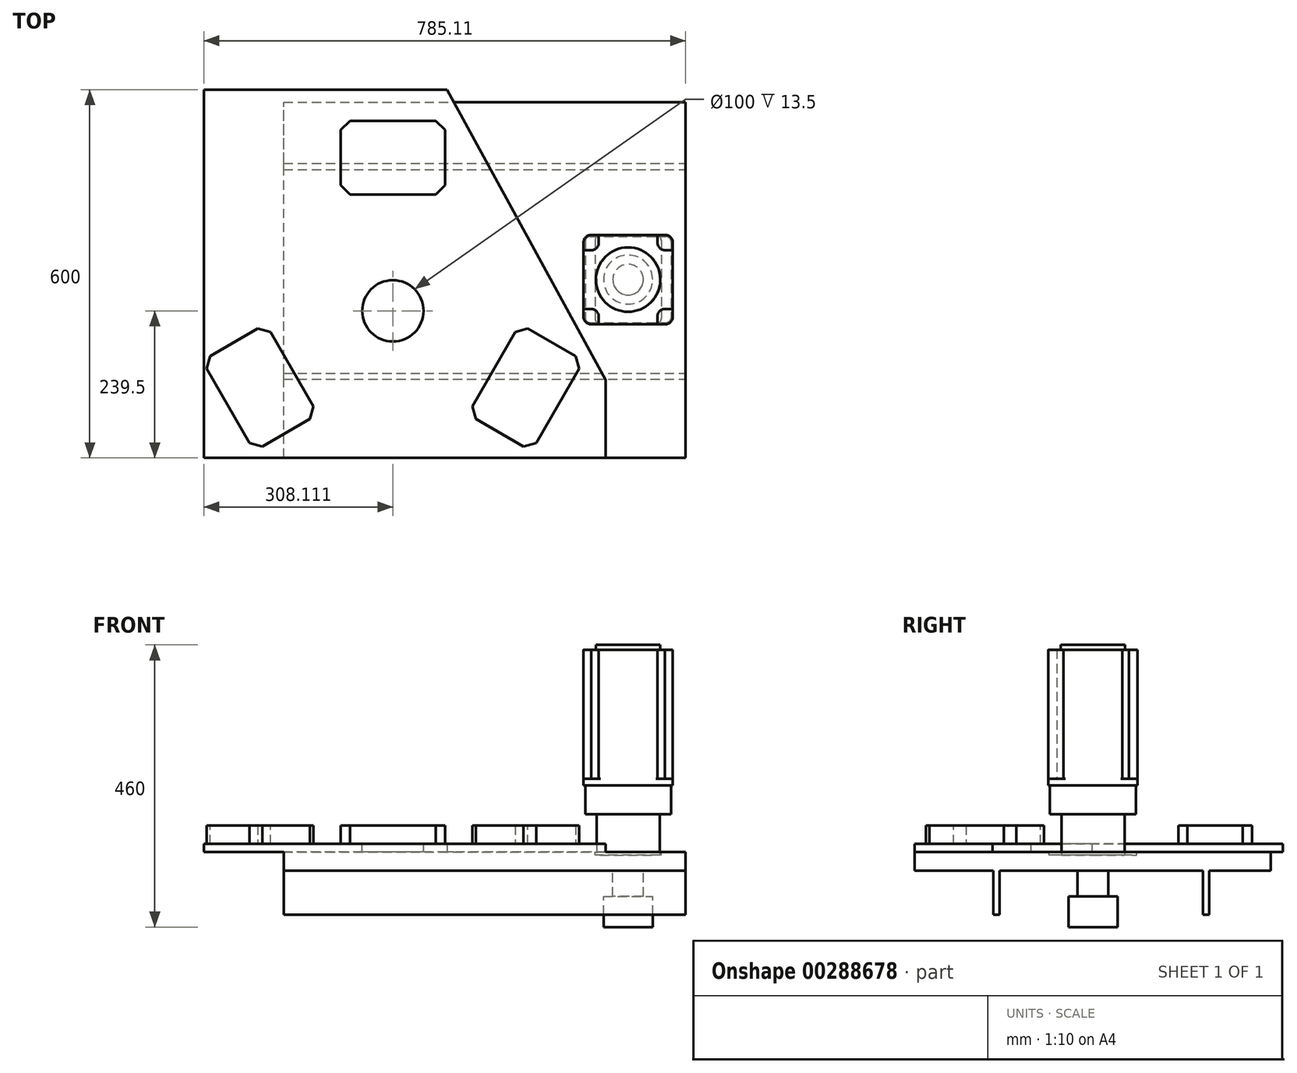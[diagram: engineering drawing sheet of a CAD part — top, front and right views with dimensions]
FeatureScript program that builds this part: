
annotation { "Feature Type Name" : "Feature", "Feature Type Description" : "" }
export const myFeature = defineFeature(function(context is Context, id is Id, definition is map)
    precondition{}
    {
        {
            var Q0;
            Q0=qCreatedBy(makeId("Front.planeOp"),FACE);
            var sketch = newSketch(context, id + "F0", { "sketchPlane" : qUnion([Q0])});
            skLineSegment(sketch, "E0.bottom", {"start": v(-291.9, 30) * mm, "end": v(363.1, 30) * mm});
            skLineSegment(sketch, "E0.top", {"start": v(-291.9, 0) * mm, "end": v(363.1, 0) * mm});
            skLineSegment(sketch, "E0.left", {"start": v(-291.9, 30) * mm, "end": v(-291.9, 0) * mm});
            skLineSegment(sketch, "E0.right", {"start": v(363.1, 30) * mm, "end": v(363.1, 0) * mm});
            skSolve(sketch);
        }
        {
            var Q0;
            Q0 = qSketchRegion(id + "F0", true);
            extrude(context, id + "F1", {"entities" : qUnion([Q0]), "depth" : 580 * mm});
        }
        {
            var Q0;
            Q0=makeQuery(id+"F1.opExtrude","SWEPT_FACE",FACE,{"disambiguationData":[OSD([sQuery(id+"F0.wireOp",EDGE,"E0.bottom")])]});
            var sketch = newSketch(context, id + "F2", { "sketchPlane" : qUnion([Q0])});
            skLineSegment(sketch, "E1.0.0", {"start": v(363.1, 0) * mm, "end": v(-291.9, 0) * mm, "construction": true});
            skLineSegment(sketch, "E1.0.1", {"start": v(-291.9, 0) * mm, "end": v(-291.9, -580) * mm, "construction": true});
            skLineSegment(sketch, "E1.0.2", {"start": v(-291.9, -580) * mm, "end": v(363.1, -580) * mm, "construction": true});
            skLineSegment(sketch, "E1.0.3", {"start": v(363.1, -580) * mm, "end": v(363.1, 0) * mm, "construction": true});
            skLineSegment(sketch, "E2", {"start": v(233.1, -580) * mm, "end": v(233.1, -453) * mm});
            skLineSegment(sketch, "E3", {"start": v(233.1, -453) * mm, "end": v(-25.85, 20) * mm});
            skLineSegment(sketch, "E4", {"start": v(-25.85, 20) * mm, "end": v(-422, 20) * mm});
            skLineSegment(sketch, "E5", {"start": v(-422, 20) * mm, "end": v(-422, -580) * mm});
            skLineSegment(sketch, "E6", {"start": v(-422, -580) * mm, "end": v(233.1, -580) * mm});
            skPoint(sketch, "E7", {"position": v(-14.9, 0) * mm});
            skSolve(sketch);
        }
        {
            var Q0;
            Q0 = qSketchRegion(id + "F2", true);
            extrude(context, id + "F3", {"entities" : qUnion([Q0]), "operationType" : NewBodyOperationType.ADD, "depth" : 13.5 * mm});
        }
        {
            var Q0;
            Q0=makeQuery(id+"F1.opExtrude","SWEPT_FACE",FACE,{"disambiguationData":[OSD([sQuery(id+"F0.wireOp",EDGE,"E0.bottom")])]});
            var sketch = newSketch(context, id + "F4", { "sketchPlane" : qUnion([Q0])});
            skLineSegment(sketch, "E8.bottom", {"start": v(223.5, -218) * mm, "end": v(315.5, -218) * mm});
            skLineSegment(sketch, "E8.top", {"start": v(223.5, -361) * mm, "end": v(315.5, -361) * mm});
            skLineSegment(sketch, "E8.left", {"start": v(215.5, -226) * mm, "end": v(215.5, -353) * mm});
            skLineSegment(sketch, "E8.right", {"start": v(323.5, -226) * mm, "end": v(323.5, -353) * mm});
            skPoint(sketch, "E9.visualSharp", {"position": v(215.5, -218) * mm});
            skArc(sketch, "E9.filletArc", {"start": v(223.5, -218) * mm, "mid": v(217.85, -220.34) * mm, "end": v(215.5, -226) * mm});
            skPoint(sketch, "E10.visualSharp", {"position": v(323.5, -218) * mm});
            skArc(sketch, "E10.filletArc", {"start": v(323.5, -226) * mm, "mid": v(321.16, -220.34) * mm, "end": v(315.5, -218) * mm});
            skPoint(sketch, "E11.visualSharp", {"position": v(323.5, -361) * mm});
            skArc(sketch, "E11.filletArc", {"start": v(315.5, -361) * mm, "mid": v(321.16, -358.66) * mm, "end": v(323.5, -353) * mm});
            skPoint(sketch, "E12.visualSharp", {"position": v(215.5, -361) * mm});
            skArc(sketch, "E12.filletArc", {"start": v(215.5, -353) * mm, "mid": v(217.85, -358.66) * mm, "end": v(223.5, -361) * mm});
            skSolve(sketch);
        }
        {
            var Q0;
            Q0 = qSketchRegion(id + "F4", true);
            extrude(context, id + "F5", {"entities" : qUnion([Q0]), "operationType" : NewBodyOperationType.REMOVE, "oppositeDirection" : true, "depth" : 5 * mm});
        }
        {
            var Q0;
            Q0=makeQuery(id+"F5.boolean.opBoolean","COPY",FACE,{"derivedFrom":makeQuery(id+"F5.opExtrude","CAP_FACE",FACE,{"disambiguationData":[OSD([sQuery(id+"F4.wireOp",EDGE,"E8.bottom"),sQuery(id+"F4.wireOp",EDGE,"E8.top"),sQuery(id+"F4.wireOp",EDGE,"E8.left"),sQuery(id+"F4.wireOp",EDGE,"E8.right"),sQuery(id+"F4.wireOp",EDGE,"E9.filletArc"),sQuery(id+"F4.wireOp",EDGE,"E10.filletArc"),sQuery(id+"F4.wireOp",EDGE,"E11.filletArc"),sQuery(id+"F4.wireOp",EDGE,"E12.filletArc")])],"isStart":false})});
            var sketch = newSketch(context, id + "F6", { "sketchPlane" : qUnion([Q0])});
            skCircle(sketch, "E13", {"center": v(269.5, -289.5) * mm, "radius": 51.5 * mm});
            skLineSegment(sketch, "E14", {"start": v(269.5, -132.8) * mm, "end": v(269.5, -446.2) * mm, "construction": true});
            skLineSegment(sketch, "E15", {"start": v(386.11, -289.5) * mm, "end": v(152.9, -289.5) * mm, "construction": true});
            skSolve(sketch);
        }
        {
            var Q0;
            Q0 = qSketchRegion(id + "F6", true);
            extrude(context, id + "F7", {"entities" : qUnion([Q0]), "operationType" : NewBodyOperationType.ADD, "depth" : 67 * mm});
        }
        {
            var Q0;
            Q0=makeQuery(id+"F7.opExtrude","CAP_FACE",FACE,{"disambiguationData":[OSD([sQuery(id+"F6.wireOp",EDGE,"E13")])],"isStart":false});
            var sketch = newSketch(context, id + "F8", { "sketchPlane" : qUnion([Q0])});
            skLineSegment(sketch, "E16.bottom", {"start": v(207.5, -219.5) * mm, "end": v(331.5, -219.5) * mm});
            skLineSegment(sketch, "E16.top", {"start": v(207.5, -359.5) * mm, "end": v(331.5, -359.5) * mm});
            skLineSegment(sketch, "E16.left", {"start": v(199.5, -227.5) * mm, "end": v(199.5, -351.5) * mm});
            skLineSegment(sketch, "E16.right", {"start": v(339.5, -227.5) * mm, "end": v(339.5, -351.5) * mm});
            skLineSegment(sketch, "E17", {"start": v(269.5, -178.35) * mm, "end": v(269.5, -446.41) * mm, "construction": true});
            skLineSegment(sketch, "E18", {"start": v(150.1, -289.5) * mm, "end": v(466.8, -289.5) * mm, "construction": true});
            skPoint(sketch, "E19.visualSharp", {"position": v(199.5, -219.5) * mm});
            skArc(sketch, "E19.filletArc", {"start": v(207.5, -219.5) * mm, "mid": v(201.85, -221.84) * mm, "end": v(199.5, -227.5) * mm});
            skPoint(sketch, "E20.visualSharp", {"position": v(339.5, -219.5) * mm});
            skArc(sketch, "E20.filletArc", {"start": v(339.5, -227.5) * mm, "mid": v(337.16, -221.84) * mm, "end": v(331.5, -219.5) * mm});
            skPoint(sketch, "E21.visualSharp", {"position": v(339.5, -359.5) * mm});
            skArc(sketch, "E21.filletArc", {"start": v(331.5, -359.5) * mm, "mid": v(337.16, -357.16) * mm, "end": v(339.5, -351.5) * mm});
            skPoint(sketch, "E22.visualSharp", {"position": v(199.5, -359.5) * mm});
            skArc(sketch, "E22.filletArc", {"start": v(199.5, -351.5) * mm, "mid": v(201.85, -357.16) * mm, "end": v(207.5, -359.5) * mm});
            skSolve(sketch);
        }
        {
            var Q0;
            Q0 = qSketchRegion(id + "F8", true);
            extrude(context, id + "F9", {"entities" : qUnion([Q0]), "operationType" : NewBodyOperationType.ADD, "depth" : 47 * mm});
        }
        {
            var Q0;
            Q0=makeQuery(id+"F9.opExtrude","CAP_FACE",FACE,{"disambiguationData":[OSD([sQuery(id+"F8.wireOp",EDGE,"E16.bottom"),sQuery(id+"F8.wireOp",EDGE,"E16.top"),sQuery(id+"F8.wireOp",EDGE,"E16.left"),sQuery(id+"F8.wireOp",EDGE,"E16.right"),sQuery(id+"F8.wireOp",EDGE,"E19.filletArc"),sQuery(id+"F8.wireOp",EDGE,"E20.filletArc"),sQuery(id+"F8.wireOp",EDGE,"E21.filletArc"),sQuery(id+"F8.wireOp",EDGE,"E22.filletArc")])],"isStart":false});
            var sketch = newSketch(context, id + "F10", { "sketchPlane" : qUnion([Q0])});
            skLineSegment(sketch, "E23.bottom", {"start": v(209.2, -216.7) * mm, "end": v(329.8, -216.7) * mm});
            skLineSegment(sketch, "E23.top", {"start": v(209.2, -362.3) * mm, "end": v(329.8, -362.3) * mm});
            skLineSegment(sketch, "E23.left", {"start": v(196.7, -229.2) * mm, "end": v(196.7, -349.8) * mm});
            skLineSegment(sketch, "E23.right", {"start": v(342.3, -229.2) * mm, "end": v(342.3, -349.8) * mm});
            skPoint(sketch, "E24.visualSharp", {"position": v(196.7, -216.7) * mm});
            skArc(sketch, "E24.filletArc", {"start": v(209.2, -216.7) * mm, "mid": v(200.37, -220.36) * mm, "end": v(196.7, -229.2) * mm});
            skPoint(sketch, "E25.visualSharp", {"position": v(342.3, -216.7) * mm});
            skArc(sketch, "E25.filletArc", {"start": v(342.3, -229.2) * mm, "mid": v(338.65, -220.36) * mm, "end": v(329.8, -216.7) * mm});
            skPoint(sketch, "E26.visualSharp", {"position": v(342.3, -362.3) * mm});
            skArc(sketch, "E26.filletArc", {"start": v(329.8, -362.3) * mm, "mid": v(338.65, -358.64) * mm, "end": v(342.3, -349.8) * mm});
            skPoint(sketch, "E27.visualSharp", {"position": v(196.7, -362.3) * mm});
            skArc(sketch, "E27.filletArc", {"start": v(196.7, -349.8) * mm, "mid": v(200.37, -358.64) * mm, "end": v(209.2, -362.3) * mm});
            skSolve(sketch);
        }
        {
            var Q0;
            Q0 = qSketchRegion(id + "F10", true);
            extrude(context, id + "F11", {"entities" : qUnion([Q0]), "operationType" : NewBodyOperationType.ADD, "depth" : 11 * mm});
        }
        {
            var Q0;
            Q0=makeQuery(id+"F11.opExtrude","CAP_FACE",FACE,{"disambiguationData":[OSD([sQuery(id+"F10.wireOp",EDGE,"E23.bottom"),sQuery(id+"F10.wireOp",EDGE,"E23.top"),sQuery(id+"F10.wireOp",EDGE,"E23.left"),sQuery(id+"F10.wireOp",EDGE,"E23.right"),sQuery(id+"F10.wireOp",EDGE,"E24.filletArc"),sQuery(id+"F10.wireOp",EDGE,"E25.filletArc"),sQuery(id+"F10.wireOp",EDGE,"E26.filletArc"),sQuery(id+"F10.wireOp",EDGE,"E27.filletArc")])],"isStart":false});
            var sketch = newSketch(context, id + "F12", { "sketchPlane" : qUnion([Q0])});
            skLineSegment(sketch, "E28.0.1", {"start": v(224.4, -362.3) * mm, "end": v(314.56, -362.3) * mm});
            skArc(sketch, "E28.0.2", {"start": v(329.8, -362.3) * mm, "mid": v(338.65, -358.64) * mm, "end": v(342.3, -349.8) * mm});
            skLineSegment(sketch, "E28.0.3", {"start": v(342.3, -334.57) * mm, "end": v(342.3, -244.44) * mm});
            skArc(sketch, "E28.0.4", {"start": v(342.3, -229.2) * mm, "mid": v(338.65, -220.36) * mm, "end": v(329.8, -216.7) * mm});
            skLineSegment(sketch, "E28.0.5", {"start": v(314.72, -216.7) * mm, "end": v(224.44, -216.7) * mm});
            skLineSegment(sketch, "E28.0.7", {"start": v(196.7, -244.44) * mm, "end": v(196.7, -334.56) * mm});
            skArc(sketch, "E29", {"start": v(208.93, -241.7) * mm, "mid": v(217.95, -238.13) * mm, "end": v(221.7, -229.18) * mm});
            skArc(sketch, "E30", {"start": v(317.46, -227.22) * mm, "mid": v(320.36, -237.39) * mm, "end": v(330, -241.7) * mm});
            skArc(sketch, "E31", {"start": v(330.3, -337.31) * mm, "mid": v(321.15, -340.79) * mm, "end": v(317.3, -349.8) * mm});
            skArc(sketch, "E32", {"start": v(221.65, -351) * mm, "mid": v(218.36, -341.28) * mm, "end": v(208.9, -337.3) * mm});
            skLineSegment(sketch, "E33", {"start": v(221.7, -229.18) * mm, "end": v(221.7, -219.45) * mm});
            skLineSegment(sketch, "E34", {"start": v(317.46, -231.18) * mm, "end": v(317.46, -219.44) * mm});
            skLineSegment(sketch, "E35", {"start": v(330, -241.7) * mm, "end": v(339.56, -241.7) * mm});
            skLineSegment(sketch, "E36", {"start": v(329.3, -337.31) * mm, "end": v(339.56, -337.31) * mm});
            skLineSegment(sketch, "E37", {"start": v(317.3, -349.8) * mm, "end": v(317.3, -359.56) * mm});
            skLineSegment(sketch, "E38", {"start": v(221.65, -348.6) * mm, "end": v(221.65, -359.56) * mm});
            skLineSegment(sketch, "E39", {"start": v(209.5, -337.3) * mm, "end": v(199.45, -337.3) * mm});
            skLineSegment(sketch, "E40", {"start": v(209.49, -241.7) * mm, "end": v(199.45, -241.7) * mm});
            skPoint(sketch, "E41.orphan", {"position": v(196.7, -229.2) * mm});
            skPoint(sketch, "E42.orphan", {"position": v(209.2, -216.7) * mm});
            skPoint(sketch, "E28.0.0.end.orphan", {"position": v(209.2, -362.3) * mm});
            skPoint(sketch, "E28.0.0.start.orphan", {"position": v(196.7, -349.8) * mm});
            skPoint(sketch, "E43.visualSharp", {"position": v(221.69, -216.7) * mm});
            skArc(sketch, "E43.filletArc", {"start": v(224.44, -216.7) * mm, "mid": v(222.5, -217.5) * mm, "end": v(221.7, -219.45) * mm});
            skPoint(sketch, "E44.visualSharp", {"position": v(317.46, -216.7) * mm});
            skArc(sketch, "E44.filletArc", {"start": v(317.46, -219.44) * mm, "mid": v(316.66, -217.5) * mm, "end": v(314.72, -216.7) * mm});
            skPoint(sketch, "E45.visualSharp", {"position": v(342.3, -241.7) * mm});
            skArc(sketch, "E45.filletArc", {"start": v(342.3, -244.44) * mm, "mid": v(341.5, -242.5) * mm, "end": v(339.56, -241.7) * mm});
            skPoint(sketch, "E46.visualSharp", {"position": v(342.3, -337.31) * mm});
            skArc(sketch, "E46.filletArc", {"start": v(339.56, -337.31) * mm, "mid": v(341.5, -336.5) * mm, "end": v(342.3, -334.57) * mm});
            skPoint(sketch, "E47.visualSharp", {"position": v(317.3, -362.3) * mm});
            skArc(sketch, "E47.filletArc", {"start": v(314.56, -362.3) * mm, "mid": v(316.5, -361.5) * mm, "end": v(317.3, -359.56) * mm});
            skPoint(sketch, "E48.visualSharp", {"position": v(221.65, -362.3) * mm});
            skArc(sketch, "E48.filletArc", {"start": v(221.65, -359.56) * mm, "mid": v(222.45, -361.5) * mm, "end": v(224.4, -362.3) * mm});
            skPoint(sketch, "E49.visualSharp", {"position": v(196.7, -337.3) * mm});
            skArc(sketch, "E49.filletArc", {"start": v(196.7, -334.56) * mm, "mid": v(197.51, -336.5) * mm, "end": v(199.45, -337.3) * mm});
            skPoint(sketch, "E50.visualSharp", {"position": v(196.7, -241.7) * mm});
            skArc(sketch, "E50.filletArc", {"start": v(199.45, -241.7) * mm, "mid": v(197.51, -242.5) * mm, "end": v(196.7, -244.44) * mm});
            skSolve(sketch);
        }
        {
            var Q0;
            Q0 = qSketchRegion(id + "F12", true);
            extrude(context, id + "F13", {"entities" : qUnion([Q0]), "operationType" : NewBodyOperationType.ADD, "depth" : (330 - 120) * mm});
        }
        {
            var Q0;
            Q0=makeQuery(id+"F13.opExtrude","CAP_FACE",FACE,{"disambiguationData":[OSD([sQuery(id+"F12.wireOp",EDGE,"E28.0.1"),sQuery(id+"F12.wireOp",EDGE,"E28.0.3"),sQuery(id+"F12.wireOp",EDGE,"E28.0.5"),sQuery(id+"F12.wireOp",EDGE,"E28.0.7"),sQuery(id+"F12.wireOp",EDGE,"E29"),sQuery(id+"F12.wireOp",EDGE,"E30"),sQuery(id+"F12.wireOp",EDGE,"E31"),sQuery(id+"F12.wireOp",EDGE,"E32"),sQuery(id+"F12.wireOp",EDGE,"E33"),sQuery(id+"F12.wireOp",EDGE,"E34"),sQuery(id+"F12.wireOp",EDGE,"E35"),sQuery(id+"F12.wireOp",EDGE,"E36"),sQuery(id+"F12.wireOp",EDGE,"E37"),sQuery(id+"F12.wireOp",EDGE,"E38"),sQuery(id+"F12.wireOp",EDGE,"E39"),sQuery(id+"F12.wireOp",EDGE,"E40"),sQuery(id+"F12.wireOp",EDGE,"E43.filletArc"),sQuery(id+"F12.wireOp",EDGE,"E44.filletArc"),sQuery(id+"F12.wireOp",EDGE,"E45.filletArc"),sQuery(id+"F12.wireOp",EDGE,"E46.filletArc"),sQuery(id+"F12.wireOp",EDGE,"E47.filletArc"),sQuery(id+"F12.wireOp",EDGE,"E48.filletArc"),sQuery(id+"F12.wireOp",EDGE,"E49.filletArc"),sQuery(id+"F12.wireOp",EDGE,"E50.filletArc")])],"isStart":false});
            var sketch = newSketch(context, id + "F14", { "sketchPlane" : qUnion([Q0])});
            skLineSegment(sketch, "E51", {"start": v(269.5, -80.34) * mm, "end": v(269.5, -491.17) * mm, "construction": true});
            skLineSegment(sketch, "E52", {"start": v(269.5, -491.17) * mm, "end": v(498.86, -289.5) * mm, "construction": true});
            skLineSegment(sketch, "E53", {"start": v(498.86, -289.5) * mm, "end": v(33.21, -289.5) * mm, "construction": true});
            skCircle(sketch, "E54", {"center": v(269.5, -289.5) * mm, "radius": 52.5 * mm});
            skSolve(sketch);
        }
        {
            var Q0;
            Q0 = qSketchRegion(id + "F14", true);
            extrude(context, id + "F15", {"entities" : qUnion([Q0]), "operationType" : NewBodyOperationType.ADD, "depth" : 8 * mm});
        }
        {
            var Q0;
            Q0=makeQuery(id+"F3.opExtrude","CAP_FACE",FACE,{"disambiguationData":[OSD([sQuery(id+"F2.wireOp",EDGE,"E2"),sQuery(id+"F2.wireOp",EDGE,"E3"),sQuery(id+"F2.wireOp",EDGE,"E4"),sQuery(id+"F2.wireOp",EDGE,"E5"),sQuery(id+"F2.wireOp",EDGE,"E6")])],"isStart":false});
            var sketch = newSketch(context, id + "F16", { "sketchPlane" : qUnion([Q0])});
            skPoint(sketch, "E55", {"position": v(-113.9, -340.5) * mm});
            skCircle(sketch, "E56", {"center": v(-113.9, -340.5) * mm, "radius": 50 * mm});
            skLineSegment(sketch, "E57.0.1", {"start": v(-291.9, 0) * mm, "end": v(-291.9, -580) * mm, "construction": true});
            skLineSegment(sketch, "E57.0.3", {"start": v(-291.9, -580) * mm, "end": v(-291.9, 0) * mm, "construction": true});
            skSolve(sketch);
        }
        {
            var Q0;
            Q0 = qSketchRegion(id + "F16", true);
            extrude(context, id + "F17", {"entities" : qUnion([Q0]), "operationType" : NewBodyOperationType.REMOVE, "oppositeDirection" : true, "depth" : 13.5 * mm});
        }
        {
            var Q0;
            Q0=makeQuery(id+"F3.opExtrude","CAP_FACE",FACE,{"disambiguationData":[OSD([sQuery(id+"F2.wireOp",EDGE,"E2"),sQuery(id+"F2.wireOp",EDGE,"E3"),sQuery(id+"F2.wireOp",EDGE,"E4"),sQuery(id+"F2.wireOp",EDGE,"E5"),sQuery(id+"F2.wireOp",EDGE,"E6")])],"isStart":false});
            var sketch = newSketch(context, id + "F18", { "sketchPlane" : qUnion([Q0])});
            skCircle(sketch, "E58.0", {"center": v(-113.9, -340.5) * mm, "radius": 50 * mm, "construction": true});
            skLineSegment(sketch, "E59", {"start": v(-113.9, -340.5) * mm, "end": v(-113.9, 54.54) * mm, "construction": true});
            skLineSegment(sketch, "E60", {"start": v(-113.9, -340.5) * mm, "end": v(225.28, -536.32) * mm, "construction": true});
            skLineSegment(sketch, "E61", {"start": v(-113.9, -340.5) * mm, "end": v(-436.6, -526.8) * mm, "construction": true});
            skPoint(sketch, "E62", {"position": v(-113.9, -90.5) * mm});
            skPoint(sketch, "E63", {"position": v(-330.4, -465.5) * mm});
            skPoint(sketch, "E64", {"position": v(102.6, -465.5) * mm});
            skLineSegment(sketch, "E65.bottom", {"start": v(-198.9, -30.5) * mm, "end": v(-28.9, -30.5) * mm});
            skLineSegment(sketch, "E65.top", {"start": v(-198.9, -150.5) * mm, "end": v(-28.9, -150.5) * mm});
            skLineSegment(sketch, "E65.left", {"start": v(-198.9, -30.5) * mm, "end": v(-198.9, -150.5) * mm});
            skLineSegment(sketch, "E65.right", {"start": v(-28.9, -30.5) * mm, "end": v(-28.9, -150.5) * mm});
            skLineSegment(sketch, "E66", {"start": v(-219.44, -90.5) * mm, "end": v(0, -90.5) * mm, "construction": true});
            skLineSegment(sketch, "E67.1.0", {"start": v(-339.87, -569.11) * mm, "end": v(-424.87, -421.89) * mm});
            skLineSegment(sketch, "E67.1.1", {"start": v(-339.87, -569.11) * mm, "end": v(-235.94, -509.11) * mm});
            skLineSegment(sketch, "E67.1.2", {"start": v(-235.94, -509.11) * mm, "end": v(-320.94, -361.89) * mm});
            skLineSegment(sketch, "E67.1.3", {"start": v(-424.87, -421.89) * mm, "end": v(-320.94, -361.89) * mm});
            skLineSegment(sketch, "E67.2.0", {"start": v(197.07, -421.89) * mm, "end": v(112.07, -569.11) * mm});
            skLineSegment(sketch, "E67.2.1", {"start": v(197.07, -421.89) * mm, "end": v(93.15, -361.89) * mm});
            skLineSegment(sketch, "E67.2.2", {"start": v(93.15, -361.89) * mm, "end": v(8.15, -509.11) * mm});
            skLineSegment(sketch, "E67.2.3", {"start": v(112.07, -569.11) * mm, "end": v(8.15, -509.11) * mm});
            skSolve(sketch);
        }
        {
            var Q0;
            Q0 = qSketchRegion(id + "F18", true);
            extrude(context, id + "F19", {"entities" : qUnion([Q0]), "operationType" : NewBodyOperationType.ADD, "depth" : 30 * mm});
        }
        {
            var Q0;
            Q0=makeQuery(id+"F19.opExtrude","SWEPT_EDGE",EDGE,{"disambiguationData":[OSD([sQuery(id+"F18.wireOp",EDGE,"E65.bottom"),sQuery(id+"F18.wireOp",EDGE,"E65.left")])]});
            chamfer(context, id + "F20", {"entities" : qUnion([Q0]), "width" : 15 * mm, "tangentPropagation" : true});
        }
        {
            var Q0;
            Q0=makeQuery(id+"F19.opExtrude","SWEPT_EDGE",EDGE,{"disambiguationData":[OSD([sQuery(id+"F18.wireOp",EDGE,"E65.bottom"),sQuery(id+"F18.wireOp",EDGE,"E65.right")])]});
            var Q1;
            Q1=makeQuery(id+"F19.opExtrude","SWEPT_EDGE",EDGE,{"disambiguationData":[OSD([sQuery(id+"F18.wireOp",EDGE,"E67.2.1"),sQuery(id+"F18.wireOp",EDGE,"E67.2.2")])]});
            var Q2;
            Q2=makeQuery(id+"F19.opExtrude","SWEPT_EDGE",EDGE,{"disambiguationData":[OSD([sQuery(id+"F18.wireOp",EDGE,"E67.2.2"),sQuery(id+"F18.wireOp",EDGE,"E67.2.3")])]});
            var Q3;
            Q3=makeQuery(id+"F19.opExtrude","SWEPT_EDGE",EDGE,{"disambiguationData":[OSD([sQuery(id+"F18.wireOp",EDGE,"E67.2.0"),sQuery(id+"F18.wireOp",EDGE,"E67.2.3")])]});
            var Q4;
            Q4=makeQuery(id+"F19.opExtrude","SWEPT_EDGE",EDGE,{"disambiguationData":[OSD([sQuery(id+"F18.wireOp",EDGE,"E67.2.0"),sQuery(id+"F18.wireOp",EDGE,"E67.2.1")])]});
            var Q5;
            Q5=makeQuery(id+"F19.opExtrude","SWEPT_EDGE",EDGE,{"disambiguationData":[OSD([sQuery(id+"F18.wireOp",EDGE,"E65.top"),sQuery(id+"F18.wireOp",EDGE,"E65.right")])]});
            var Q6;
            Q6=makeQuery(id+"F19.opExtrude","SWEPT_EDGE",EDGE,{"disambiguationData":[OSD([sQuery(id+"F18.wireOp",EDGE,"E65.top"),sQuery(id+"F18.wireOp",EDGE,"E65.left")])]});
            var Q7;
            Q7=makeQuery(id+"F19.opExtrude","SWEPT_EDGE",EDGE,{"disambiguationData":[OSD([sQuery(id+"F18.wireOp",EDGE,"E67.1.1"),sQuery(id+"F18.wireOp",EDGE,"E67.1.2")])]});
            var Q8;
            Q8=makeQuery(id+"F19.opExtrude","SWEPT_EDGE",EDGE,{"disambiguationData":[OSD([sQuery(id+"F18.wireOp",EDGE,"E67.1.0"),sQuery(id+"F18.wireOp",EDGE,"E67.1.1")])]});
            var Q9;
            Q9=makeQuery(id+"F19.opExtrude","SWEPT_EDGE",EDGE,{"disambiguationData":[OSD([sQuery(id+"F18.wireOp",EDGE,"E67.1.0"),sQuery(id+"F18.wireOp",EDGE,"E67.1.3")])]});
            var Q10;
            Q10=makeQuery(id+"F19.opExtrude","SWEPT_EDGE",EDGE,{"disambiguationData":[OSD([sQuery(id+"F18.wireOp",EDGE,"E67.1.2"),sQuery(id+"F18.wireOp",EDGE,"E67.1.3")])]});
            chamfer(context, id + "F21", {"entities" : qUnion([Q0, Q1, Q2, Q3, Q4, Q5, Q6, Q7, Q8, Q9, Q10]), "width" : 15 * mm, "tangentPropagation" : true});
        }
        {
            var Q0;
            Q0=makeQuery(id+"F1.opExtrude","SWEPT_FACE",FACE,{"disambiguationData":[OSD([sQuery(id+"F0.wireOp",EDGE,"E0.top")])]});
            var sketch = newSketch(context, id + "F22", { "sketchPlane" : qUnion([Q0])});
            skLineSegment(sketch, "E68.bottom", {"start": v(-291.9, 110) * mm, "end": v(363.1, 110) * mm});
            skLineSegment(sketch, "E68.top", {"start": v(-291.9, 100) * mm, "end": v(363.1, 100) * mm});
            skLineSegment(sketch, "E68.left", {"start": v(-291.9, 110) * mm, "end": v(-291.9, 100) * mm});
            skLineSegment(sketch, "E68.right", {"start": v(363.1, 110) * mm, "end": v(363.1, 100) * mm});
            skLineSegment(sketch, "E69.bottom", {"start": v(-291.9, 452) * mm, "end": v(363.1, 452) * mm});
            skLineSegment(sketch, "E69.top", {"start": v(-291.9, 442) * mm, "end": v(363.1, 442) * mm});
            skLineSegment(sketch, "E69.left", {"start": v(-291.9, 452) * mm, "end": v(-291.9, 442) * mm});
            skLineSegment(sketch, "E69.right", {"start": v(363.1, 452) * mm, "end": v(363.1, 442) * mm});
            skSolve(sketch);
        }
        {
            var Q0;
            Q0 = qSketchRegion(id + "F22", true);
            extrude(context, id + "F23", {"entities" : qUnion([Q0]), "operationType" : NewBodyOperationType.ADD, "depth" : (101.7 - 30) * mm});
        }
        {
            var Q0;
            Q0=makeQuery(id+"F23.boolean.opBoolean","SPLIT",FACE,{"disambiguationData":[TD([makeQuery(id+"F23.opExtrude","SWEPT_FACE",FACE,{"disambiguationData":[OSD([sQuery(id+"F22.wireOp",EDGE,"E68.bottom")])]})])],"derivedFrom":makeQuery(id+"F1.opExtrude","SWEPT_FACE",FACE,{"disambiguationData":[OSD([sQuery(id+"F0.wireOp",EDGE,"E0.top")])]})});
            var sketch = newSketch(context, id + "F24", { "sketchPlane" : qUnion([Q0])});
            skCircle(sketch, "E70.0", {"center": v(269.5, 289.5) * mm, "radius": 51.5 * mm, "construction": true});
            skCircle(sketch, "E71", {"center": v(269.5, 289.5) * mm, "radius": 25 * mm});
            skSolve(sketch);
        }
        {
            var Q0;
            Q0 = qSketchRegion(id + "F24", true);
            extrude(context, id + "F25", {"entities" : qUnion([Q0]), "operationType" : NewBodyOperationType.ADD, "depth" : 42 * mm});
        }
        {
            var Q0;
            Q0=makeQuery(id+"F25.opExtrude","CAP_FACE",FACE,{"disambiguationData":[OSD([sQuery(id+"F24.wireOp",EDGE,"E71")])],"isStart":false});
            var sketch = newSketch(context, id + "F26", { "sketchPlane" : qUnion([Q0])});
            skCircle(sketch, "E72", {"center": v(269.5, 289.5) * mm, "radius": 40 * mm});
            skSolve(sketch);
        }
        {
            var Q0;
            Q0 = qSketchRegion(id + "F26", true);
            extrude(context, id + "F27", {"entities" : qUnion([Q0]), "operationType" : NewBodyOperationType.ADD, "depth" : 50 * mm});
        }
    });
